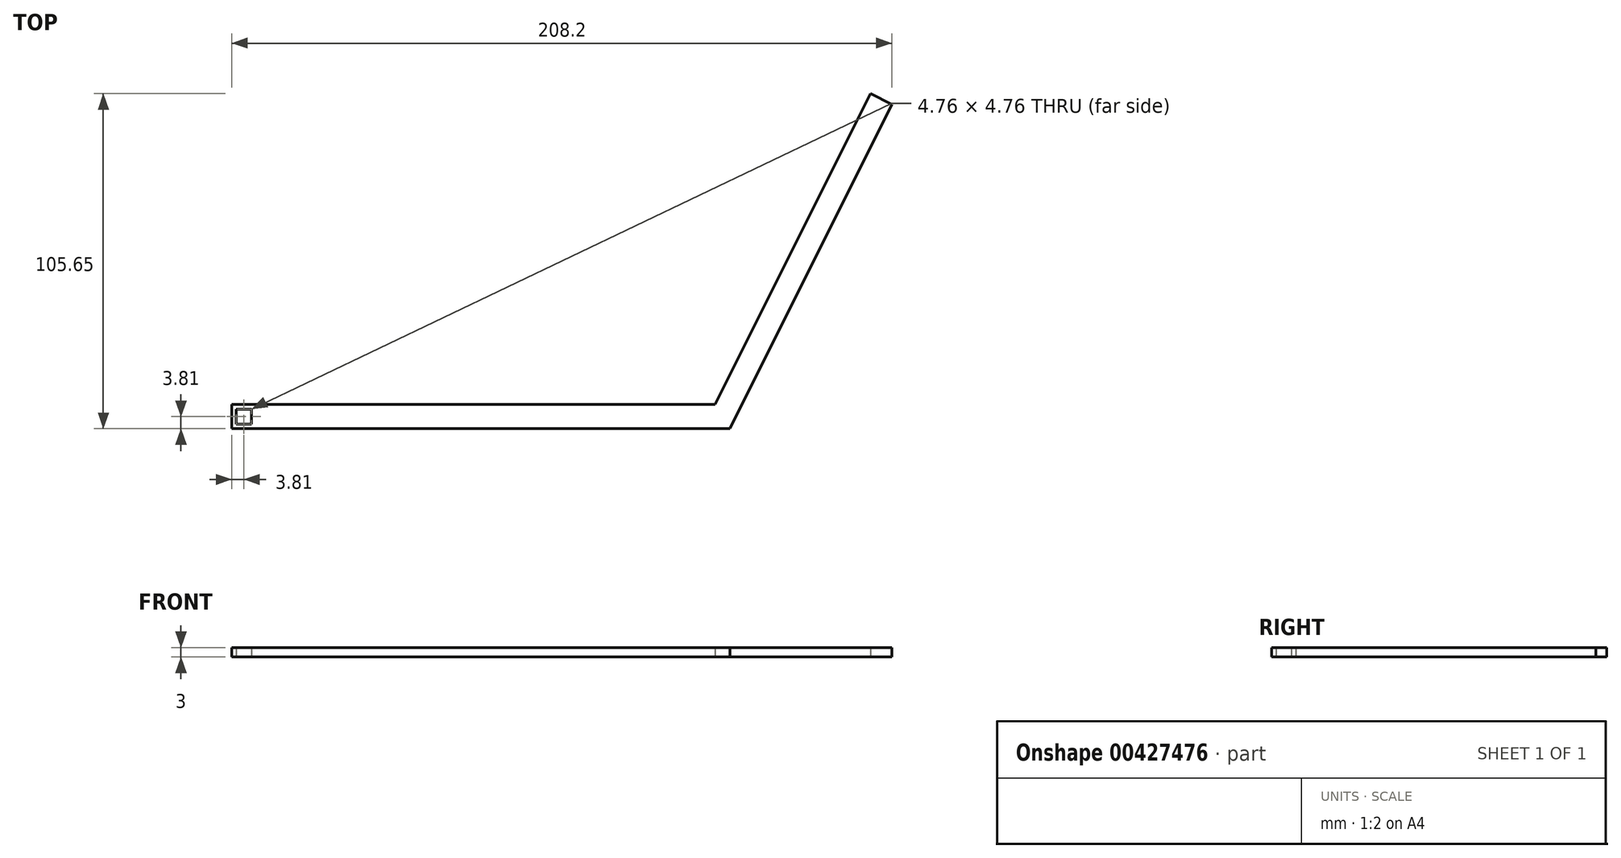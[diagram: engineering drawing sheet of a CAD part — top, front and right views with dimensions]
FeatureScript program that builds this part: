
annotation { "Feature Type Name" : "Feature", "Feature Type Description" : "" }
export const myFeature = defineFeature(function(context is Context, id is Id, definition is map)
    precondition{}
    {
        {
            var Q0;
            Q0=qCreatedBy(makeId("Top.planeOp"),FACE);
            var sketch = newSketch(context, id + "F0", { "sketchPlane" : qUnion([Q0])});
            skLineSegment(sketch, "E0", {"start": v(0, 0) * mm, "end": v(0, 7.62) * mm});
            skLineSegment(sketch, "E1", {"start": v(0, 7.62) * mm, "end": v(152.4, 7.62) * mm});
            skLineSegment(sketch, "E2", {"start": v(152.4, 7.62) * mm, "end": v(201.38, 105.65) * mm});
            skLineSegment(sketch, "E3", {"start": v(201.38, 105.65) * mm, "end": v(208.2, 102.25) * mm});
            skLineSegment(sketch, "E4", {"start": v(208.2, 102.25) * mm, "end": v(157.11, 0) * mm});
            skLineSegment(sketch, "E5", {"start": v(157.11, 0) * mm, "end": v(0, 0) * mm});
            skLineSegment(sketch, "E6.bottom", {"start": v(1.43, 6.2) * mm, "end": v(6.2, 6.2) * mm});
            skLineSegment(sketch, "E6.top", {"start": v(1.43, 1.43) * mm, "end": v(6.2, 1.43) * mm});
            skLineSegment(sketch, "E6.left", {"start": v(1.43, 6.2) * mm, "end": v(1.43, 1.43) * mm});
            skLineSegment(sketch, "E6.right", {"start": v(6.2, 6.2) * mm, "end": v(6.2, 1.43) * mm});
            skPoint(sketch, "E7", {"position": v(1.43, 3.81) * mm});
            skPoint(sketch, "E8", {"position": v(0, 3.81) * mm});
            skSolve(sketch);
        }
        {
            var Q0;
            Q0=makeQuery(id+"F0.imprint","IMPRINT",FACE,{"disambiguationData":[TD([[makeQuery(id+"F0.imprint","IMPRINT",EDGE,{"derivedFrom":sQuery(id+"F0.wireOp",EDGE,"E0")}),-1.0]])]});
            extrude(context, id + "F1", {"entities" : qUnion([Q0]), "depth" : 3 * mm});
        }
    });
